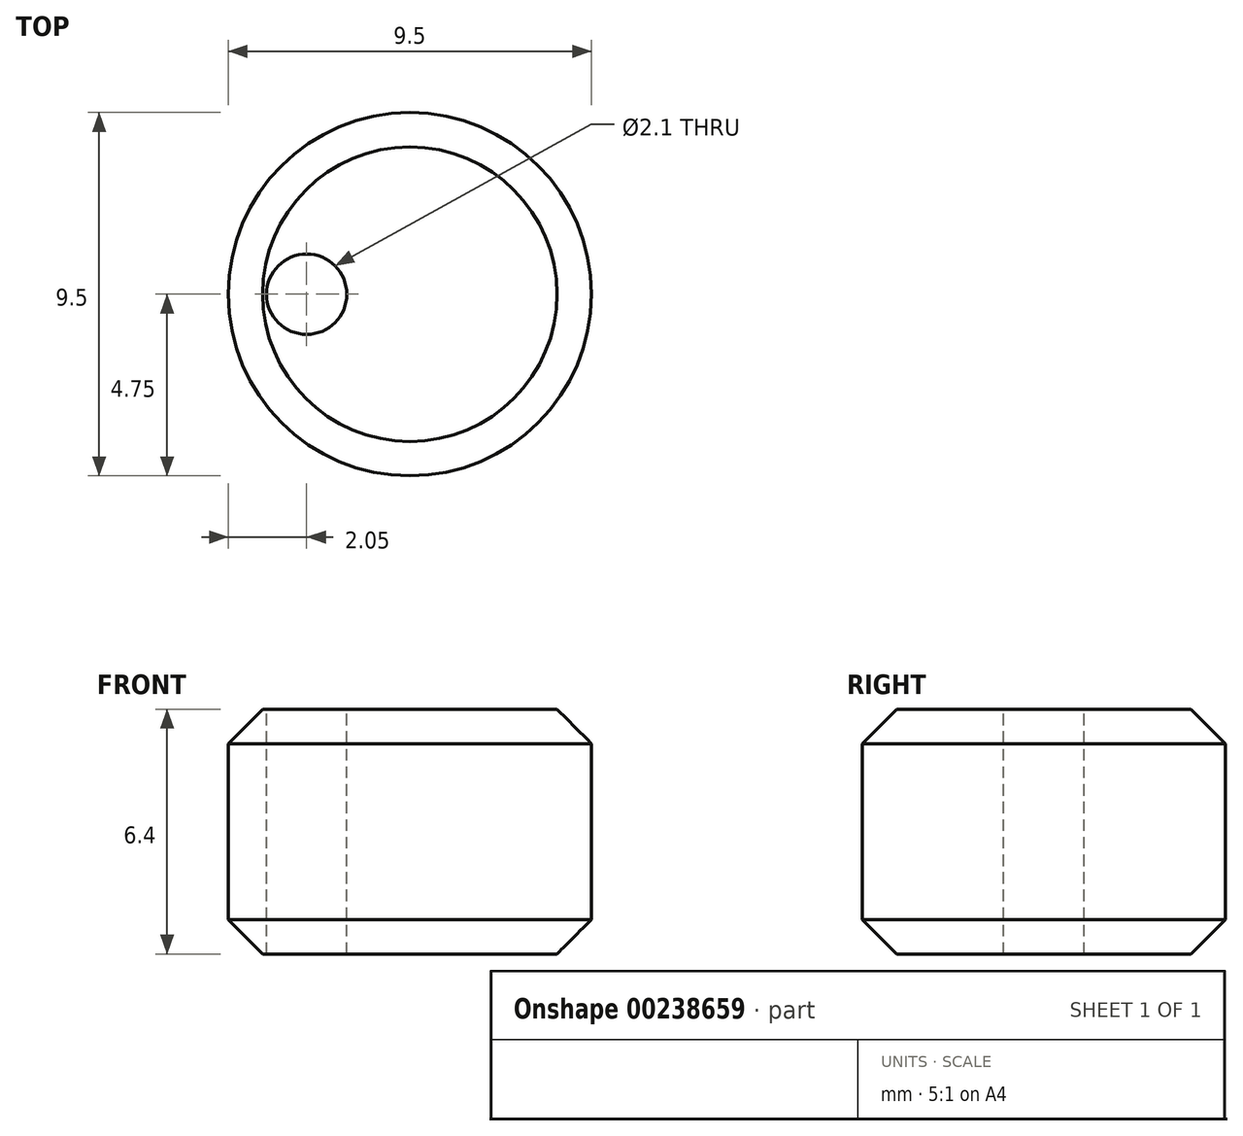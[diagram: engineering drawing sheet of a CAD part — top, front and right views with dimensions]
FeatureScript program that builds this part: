
annotation { "Feature Type Name" : "Feature", "Feature Type Description" : "" }
export const myFeature = defineFeature(function(context is Context, id is Id, definition is map)
    precondition{}
    {
        {
            var Q0;
            Q0=qCreatedBy(makeId("Top.planeOp"),FACE);
            var sketch = newSketch(context, id + "F0", { "sketchPlane" : qUnion([Q0])});
            skCircle(sketch, "E0", {"center": v(0, 0) * mm, "radius": 4.75 * mm});
            skSolve(sketch);
        }
        {
            var Q0;
            Q0 = qSketchRegion(id + "F0", true);
            extrude(context, id + "F1", {"entities" : qUnion([Q0]), "depth" : 6.4 * mm});
        }
        {
            var Q0;
            Q0=makeQuery(id+"F1.opExtrude","CAP_FACE",FACE,{"disambiguationData":[OSD([sQuery(id+"F0.wireOp",EDGE,"E0")])],"isStart":false});
            var sketch = newSketch(context, id + "F2", { "sketchPlane" : qUnion([Q0])});
            skCircle(sketch, "E1", {"center": v(-2.7, 0) * mm, "radius": 1.05 * mm});
            skSolve(sketch);
        }
        {
            var Q0;
            Q0=makeQuery(id+"F2.imprint","IMPRINT",FACE,{"disambiguationData":[TD([[makeQuery(id+"F2.imprint","IMPRINT",EDGE,{"derivedFrom":sQuery(id+"F2.wireOp",EDGE,"E1")}),1.0]])]});
            var Q1;
            Q1=sQuery(id+"F2.wireOp",EDGE,"E1");
            extrude(context, id + "F3", {"entities" : qUnion([Q0]), "operationType" : NewBodyOperationType.REMOVE, "surfaceEntities" : qUnion([Q1]), "endBound" : BoundingType.THROUGH_ALL, "oppositeDirection" : true, "depth" : 25 * mm});
        }
        {
            var Q0;
            Q0=makeQuery(id+"F1.opExtrude","CAP_EDGE",EDGE,{"disambiguationData":[OSD([sQuery(id+"F0.wireOp",EDGE,"E0")])],"isStart":false});
            var Q1;
            Q1=makeQuery(id+"F1.opExtrude","CAP_EDGE",EDGE,{"disambiguationData":[OSD([sQuery(id+"F0.wireOp",EDGE,"E0")])],"isStart":true});
            chamfer(context, id + "F4", {"entities" : qUnion([Q0, Q1]), "width" : .9 * mm, "tangentPropagation" : true});
        }
    });
